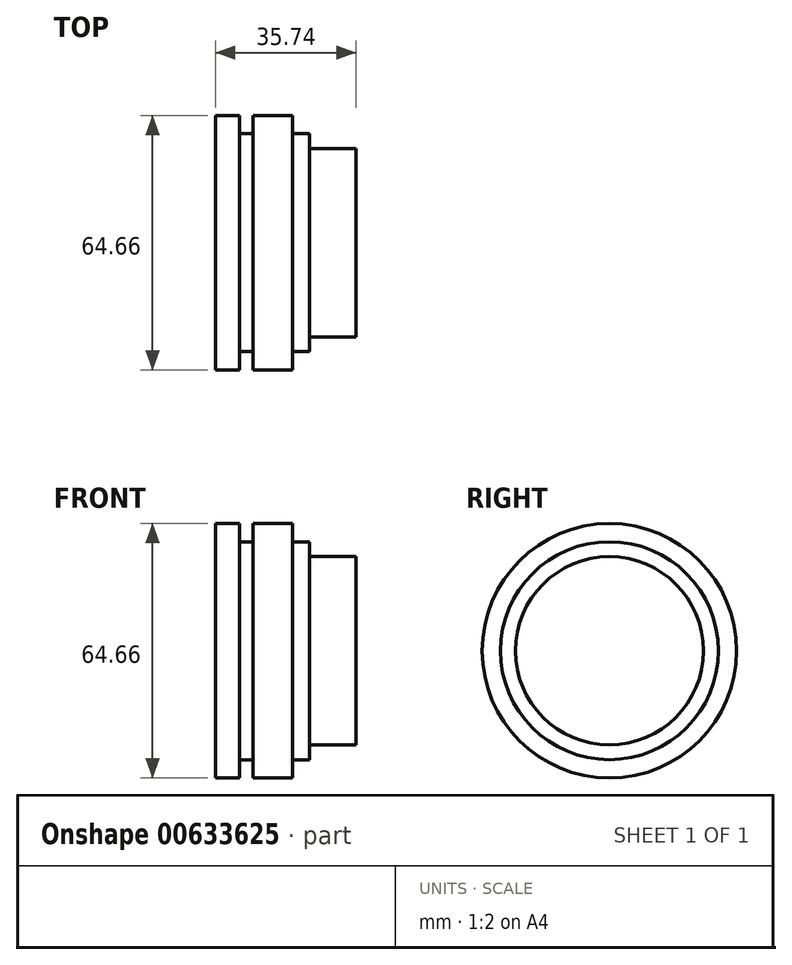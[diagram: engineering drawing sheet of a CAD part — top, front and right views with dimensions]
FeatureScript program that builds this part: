
annotation { "Feature Type Name" : "Feature", "Feature Type Description" : "" }
export const myFeature = defineFeature(function(context is Context, id is Id, definition is map)
    precondition{}
    {
        {
            var Q0;
            Q0=qCreatedBy(makeId("Front.planeOp"),FACE);
            var sketch = newSketch(context, id + "F0", { "sketchPlane" : qUnion([Q0])});
            skLineSegment(sketch, "E0", {"start": v(-19.54, 0) * mm, "end": v(-19.54, 32.33) * mm});
            skLineSegment(sketch, "E1", {"start": v(-19.54, 32.33) * mm, "end": v(-13.44, 32.33) * mm});
            skLineSegment(sketch, "E2", {"start": v(-13.44, 32.33) * mm, "end": v(-13.44, 27.68) * mm});
            skLineSegment(sketch, "E3", {"start": v(-13.44, 27.68) * mm, "end": v(-9.95, 27.68) * mm});
            skLineSegment(sketch, "E4", {"start": v(-9.95, 27.68) * mm, "end": v(-9.95, 32.33) * mm});
            skLineSegment(sketch, "E5", {"start": v(-9.95, 32.33) * mm, "end": v(0, 32.33) * mm});
            skLineSegment(sketch, "E6", {"start": v(0, 32.33) * mm, "end": v(0, 27.68) * mm});
            skLineSegment(sketch, "E7", {"start": v(0, 27.68) * mm, "end": v(4.29, 27.68) * mm});
            skLineSegment(sketch, "E8", {"start": v(4.29, 27.68) * mm, "end": v(4.29, 23.9) * mm});
            skLineSegment(sketch, "E9", {"start": v(4.29, 23.9) * mm, "end": v(16.2, 23.9) * mm});
            skLineSegment(sketch, "E10", {"start": v(16.2, 23.9) * mm, "end": v(16.2, 0) * mm});
            skLineSegment(sketch, "E11", {"start": v(16.2, 0) * mm, "end": v(-19.54, 0) * mm});
            skSolve(sketch);
        }
        {
            var Q0;
            Q0=makeQuery(id+"F0.imprint","IMPRINT",FACE,{"disambiguationData":[TD([[makeQuery(id+"F0.imprint","IMPRINT",EDGE,{"derivedFrom":sQuery(id+"F0.wireOp",EDGE,"E0")}),-1.0]])]});
            var Q1;
            Q1=sQuery(id+"F0.wireOp",EDGE,"E11");
            revolve(context, id + "F1", {"entities" : qUnion([Q0]), "axis" : qUnion([Q1]), "revolveType" : RevolveType.FULL});
        }
    });
